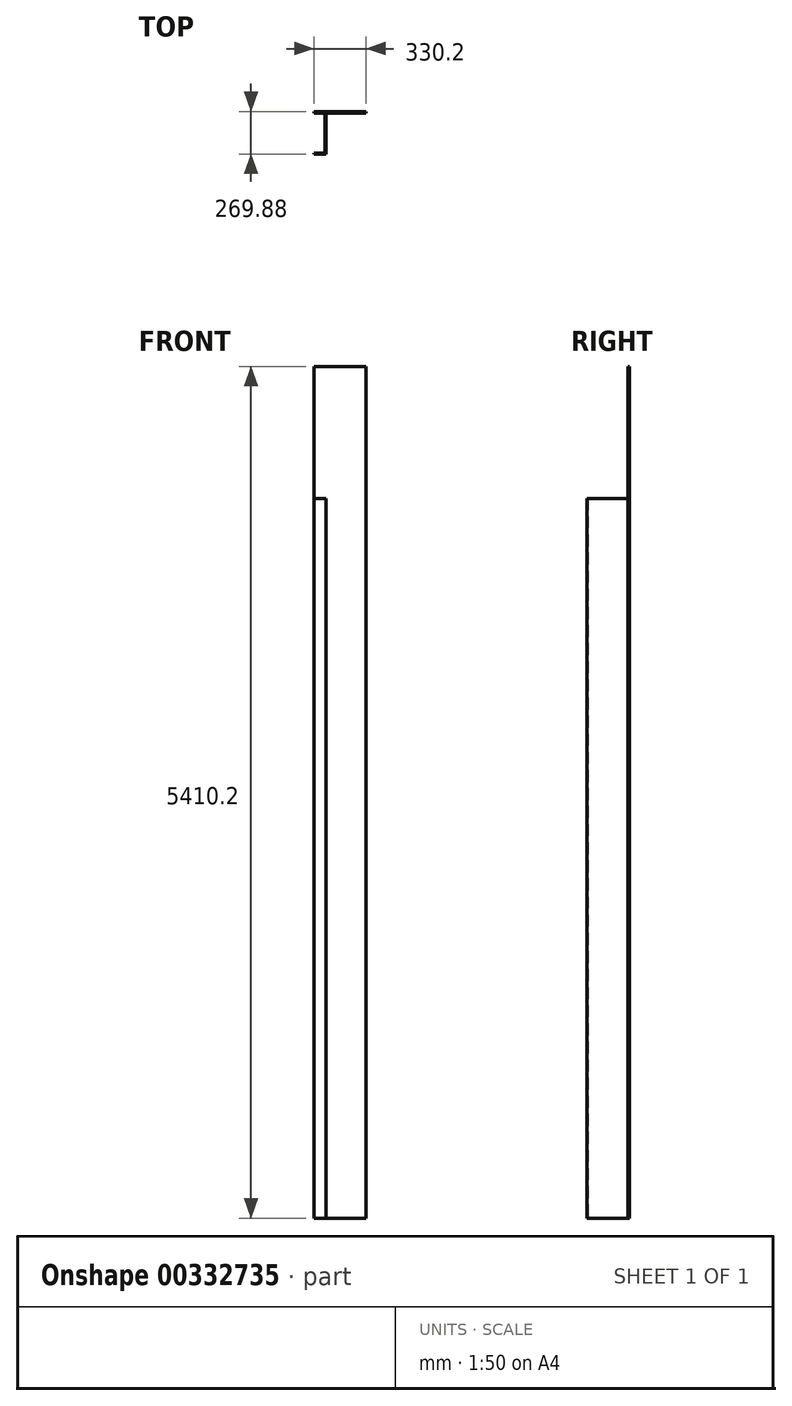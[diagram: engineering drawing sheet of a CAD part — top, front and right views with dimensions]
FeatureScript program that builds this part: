
annotation { "Feature Type Name" : "Feature", "Feature Type Description" : "" }
export const myFeature = defineFeature(function(context is Context, id is Id, definition is map)
    precondition{}
    {
        {
            var Q0;
            Q0=qCreatedBy(makeId("Top.planeOp"),FACE);
            var sketch = newSketch(context, id + "F0", { "sketchPlane" : qUnion([Q0])});
            skLineSegment(sketch, "E0", {"start": v(0, 0) * mm, "end": v(76.2, 0) * mm});
            skLineSegment(sketch, "E1", {"start": v(76.2, 0) * mm, "end": v(76.2, 260.35) * mm});
            skLineSegment(sketch, "E2", {"start": v(76.2, 260.35) * mm, "end": v(330.2, 260.35) * mm});
            skLineSegment(sketch, "E3", {"start": v(330.2, 260.35) * mm, "end": v(330.2, 269.88) * mm});
            skLineSegment(sketch, "E4", {"start": v(330.2, 269.88) * mm, "end": v(0, 269.88) * mm});
            skLineSegment(sketch, "E5", {"start": v(0, 269.88) * mm, "end": v(0, 260.35) * mm});
            skLineSegment(sketch, "E6", {"start": v(0, 260.35) * mm, "end": v(69.85, 260.35) * mm});
            skLineSegment(sketch, "E7", {"start": v(69.85, 260.35) * mm, "end": v(69.85, 6.35) * mm});
            skLineSegment(sketch, "E8", {"start": v(69.85, 6.35) * mm, "end": v(0, 6.35) * mm});
            skLineSegment(sketch, "E9", {"start": v(0, 6.35) * mm, "end": v(0, 0) * mm});
            skSolve(sketch);
        }
        {
            var Q0;
            Q0 = qSketchRegion(id + "F0", true);
            extrude(context, id + "F1", {"entities" : qUnion([Q0]), "depth" : 4572 * mm});
        }
        {
            var Q0;
            Q0=makeQuery(id+"F1.opExtrude","CAP_FACE",FACE,{"disambiguationData":[OSD([sQuery(id+"F0.wireOp",EDGE,"E0"),sQuery(id+"F0.wireOp",EDGE,"E1"),sQuery(id+"F0.wireOp",EDGE,"E2"),sQuery(id+"F0.wireOp",EDGE,"E3"),sQuery(id+"F0.wireOp",EDGE,"E4"),sQuery(id+"F0.wireOp",EDGE,"E5"),sQuery(id+"F0.wireOp",EDGE,"E6"),sQuery(id+"F0.wireOp",EDGE,"E7"),sQuery(id+"F0.wireOp",EDGE,"E8"),sQuery(id+"F0.wireOp",EDGE,"E9")])],"isStart":false});
            var sketch = newSketch(context, id + "F2", { "sketchPlane" : qUnion([Q0])});
            skLineSegment(sketch, "E10.bottom", {"start": v(0, 269.88) * mm, "end": v(330.2, 269.88) * mm});
            skLineSegment(sketch, "E10.top", {"start": v(0, 260.35) * mm, "end": v(330.2, 260.35) * mm});
            skLineSegment(sketch, "E10.left", {"start": v(0, 269.88) * mm, "end": v(0, 260.35) * mm});
            skLineSegment(sketch, "E10.right", {"start": v(330.2, 269.88) * mm, "end": v(330.2, 260.35) * mm});
            skSolve(sketch);
        }
        {
            var Q0;
            Q0=makeQuery(id+"F2.imprint","IMPRINT",FACE,{"disambiguationData":[TD([[makeQuery(id+"F2.imprint","IMPRINT",EDGE,{"derivedFrom":sQuery(id+"F2.wireOp",EDGE,"E10.bottom")}),1.0]])]});
            extrude(context, id + "F3", {"entities" : qUnion([Q0]), "operationType" : NewBodyOperationType.ADD, "depth" : 838.2 * mm});
        }
    });
